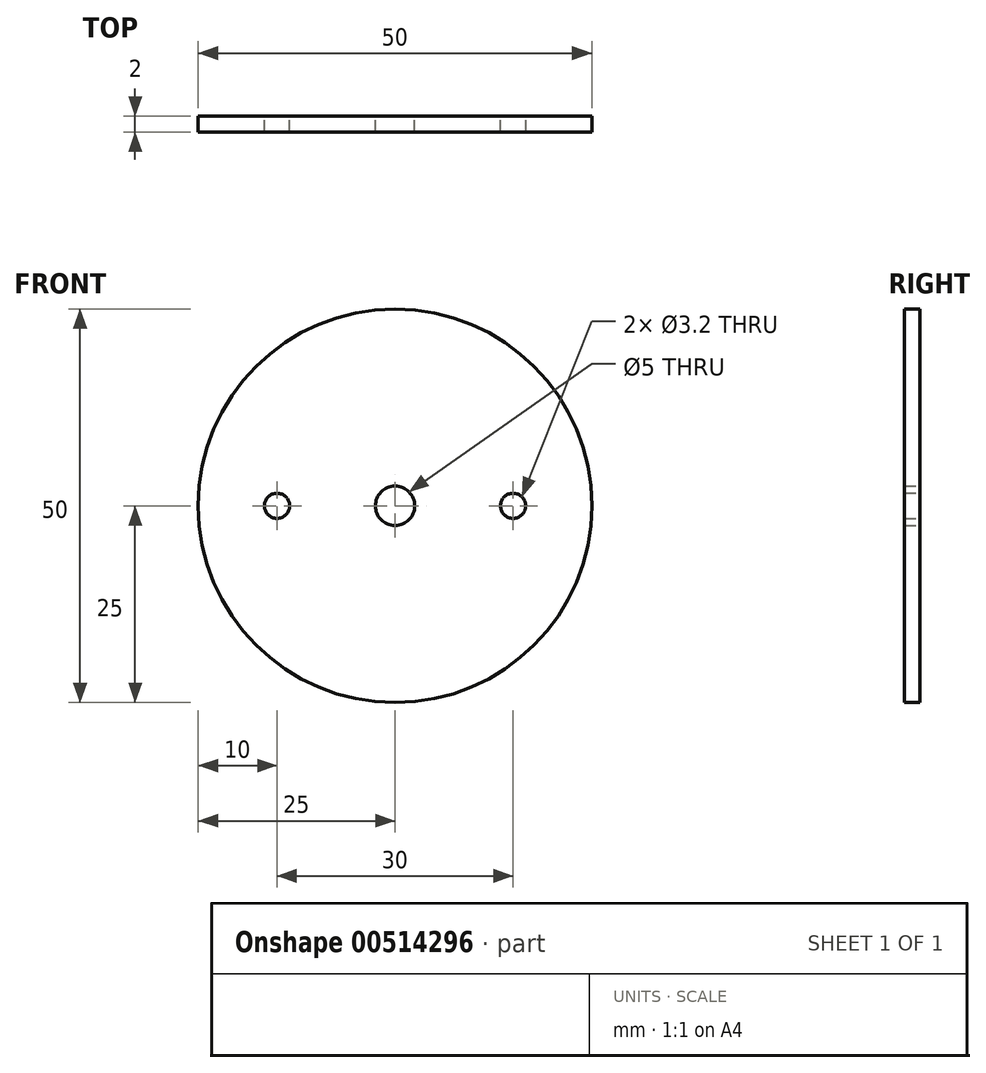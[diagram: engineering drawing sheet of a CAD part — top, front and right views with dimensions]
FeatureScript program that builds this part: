
annotation { "Feature Type Name" : "Feature", "Feature Type Description" : "" }
export const myFeature = defineFeature(function(context is Context, id is Id, definition is map)
    precondition{}
    {
        {
            var Q0;
            Q0=qCreatedBy(makeId("Front.planeOp"),FACE);
            var sketch = newSketch(context, id + "F0", { "sketchPlane" : qUnion([Q0])});
            skCircle(sketch, "E0", {"center": v(0, 0) * mm, "radius": 25 * mm});
            skCircle(sketch, "E1", {"center": v(0, 0) * mm, "radius": 2.5 * mm});
            skCircle(sketch, "E2", {"center": v(-15, 0) * mm, "radius": 1.6 * mm});
            skLineSegment(sketch, "E3", {"start": v(0, -39.17) * mm, "end": v(0, 26.61) * mm, "construction": true});
            skCircle(sketch, "E4.MirrorC", {"center": v(15, 0) * mm, "radius": 1.6 * mm});
            skSolve(sketch);
        }
        {
            var Q0;
            Q0 = qSketchRegion(id + "F0", true);
            extrude(context, id + "F1", {"entities" : qUnion([Q0]), "depth" : 2 * mm, "offsetDistance" : 25 * mm});
        }
    });
